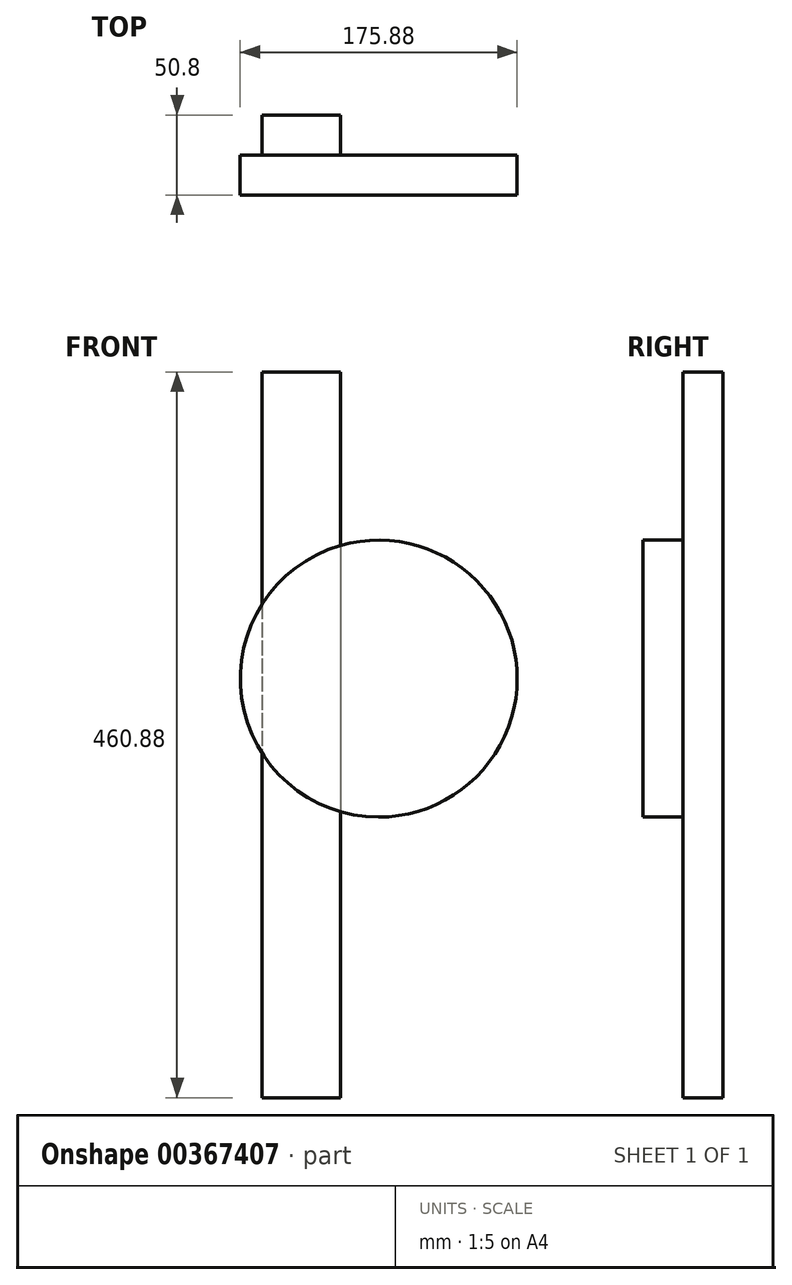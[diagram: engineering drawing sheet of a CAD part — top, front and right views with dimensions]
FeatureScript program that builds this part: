
annotation { "Feature Type Name" : "Feature", "Feature Type Description" : "" }
export const myFeature = defineFeature(function(context is Context, id is Id, definition is map)
    precondition{}
    {
        {
            var Q0;
            Q0=qCreatedBy(makeId("Front.planeOp"),FACE);
            var sketch = newSketch(context, id + "F0", { "sketchPlane" : qUnion([Q0])});
            skCircle(sketch, "E0", {"center": v(0, 0) * mm, "radius": 87.94 * mm});
            skSolve(sketch);
        }
        {
            var Q0;
            Q0=makeQuery(id+"F0.imprint","IMPRINT",FACE,{"disambiguationData":[TD([[makeQuery(id+"F0.imprint","IMPRINT",EDGE,{"derivedFrom":sQuery(id+"F0.wireOp",EDGE,"E0")}),1.0]])]});
            extrude(context, id + "F1", {"entities" : qUnion([Q0]), "depth" : 25.4 * mm});
        }
        {
            var Q0;
            Q0=makeQuery(id+"F1.opExtrude","CAP_FACE",FACE,{"disambiguationData":[OSD([sQuery(id+"F0.wireOp",EDGE,"E0")])],"isStart":true});
            var sketch = newSketch(context, id + "F2", { "sketchPlane" : qUnion([Q0])});
            skLineSegment(sketch, "E1.bottom", {"start": v(24.35, 194.74) * mm, "end": v(74.14, 194.74) * mm});
            skLineSegment(sketch, "E1.top", {"start": v(24.35, -266.14) * mm, "end": v(74.14, -266.14) * mm});
            skLineSegment(sketch, "E1.left", {"start": v(24.35, 194.74) * mm, "end": v(24.35, -266.14) * mm});
            skLineSegment(sketch, "E1.right", {"start": v(74.14, 194.74) * mm, "end": v(74.14, -266.14) * mm});
            skPoint(sketch, "E1.middle", {"position": v(49.25, -35.7) * mm});
            skSolve(sketch);
        }
        {
            var Q0;
            {var subQ0=sQuery(id+"F2.wireOp",EDGE,"E1.left");var subQ1=makeQuery(id+"F1.opExtrude","CAP_EDGE",EDGE,{"disambiguationData":[OSD([sQuery(id+"F0.wireOp",EDGE,"E0")])],"isStart":true});var subQ2=makeQuery(id+"F2.imprint","INTERSECT",VERTEX,{"disambiguationData":[OD(0.0)],"derivedFrom":[subQ1,subQ0]});Q0=makeQuery(id+"F2.imprint","IMPRINT",FACE,{"disambiguationData":[TD([[makeQuery(id+"F2.imprint","IMPRINT",EDGE,{"disambiguationData":[TD([[subQ2,-1.0]])],"derivedFrom":subQ0}),1.0]])]});}
            var Q1;
            {var subQ0=sQuery(id+"F2.wireOp",EDGE,"E1.bottom");Q1=makeQuery(id+"F2.imprint","IMPRINT",FACE,{"disambiguationData":[TD([[makeQuery(id+"F2.imprint","IMPRINT",EDGE,{"derivedFrom":subQ0}),-1.0]])]});}
            var Q2;
            {var subQ0=sQuery(id+"F2.wireOp",EDGE,"E1.top");Q2=makeQuery(id+"F2.imprint","IMPRINT",FACE,{"disambiguationData":[TD([[makeQuery(id+"F2.imprint","IMPRINT",EDGE,{"derivedFrom":subQ0}),1.0]])]});}
            var Q3;
            Q3 = qSketchRegion(id + "F2", true);
            extrude(context, id + "F3", {"entities" : qUnion([Q0, Q1, Q2, Q3]), "operationType" : NewBodyOperationType.ADD, "depth" : 25.4 * mm});
        }
    });
